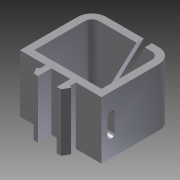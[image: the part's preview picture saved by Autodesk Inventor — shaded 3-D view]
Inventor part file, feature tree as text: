
AUTODESK INVENTOR PART (.ipt)
format: ipt  version: 2012 (Build 160160000, 160)  size: 153,088 bytes
history: native  units: mm
features: extrude x3, sketch x3
ambient origin geometry x8: Origin, YZ Plane, XZ Plane, XY Plane, X Axis, Y Axis, Z Axis, Center Point
bodies: Solid1 (feature_tree)
feature tree (6):
  extrude  "Extrusion1"  Depth=2.8mm
  extrude  "Extrusion2"  Depth=12.0mm TaperAngle=0.0deg
  extrude  "Extrusion3"  Depth=1.5mm
  sketch  "Sketch1"  dims[d1=1.2mm d2=1.95mm d3=120.0deg d5=8.5mm d6=1.5mm d8=1.5mm d9=12.0mm d10=3.0mm d11=1.5mm d12=0.9mm d13=120.0deg d14=2.8mm d15=1.2mm d16=2.8mm]
  sketch  "Sketch2"  dims[d17=1.5mm d18=12.0mm d19=0.0mm]
  sketch  "Sketch3"  dims[d20=1.5mm d21=1.5mm d22=1.5mm d23=0.0mm d24=0.0mm d28=0.0mm d29=0.0mm d30=1.5mm d31=3.5mm d32=4.25mm d33=2.0mm]
